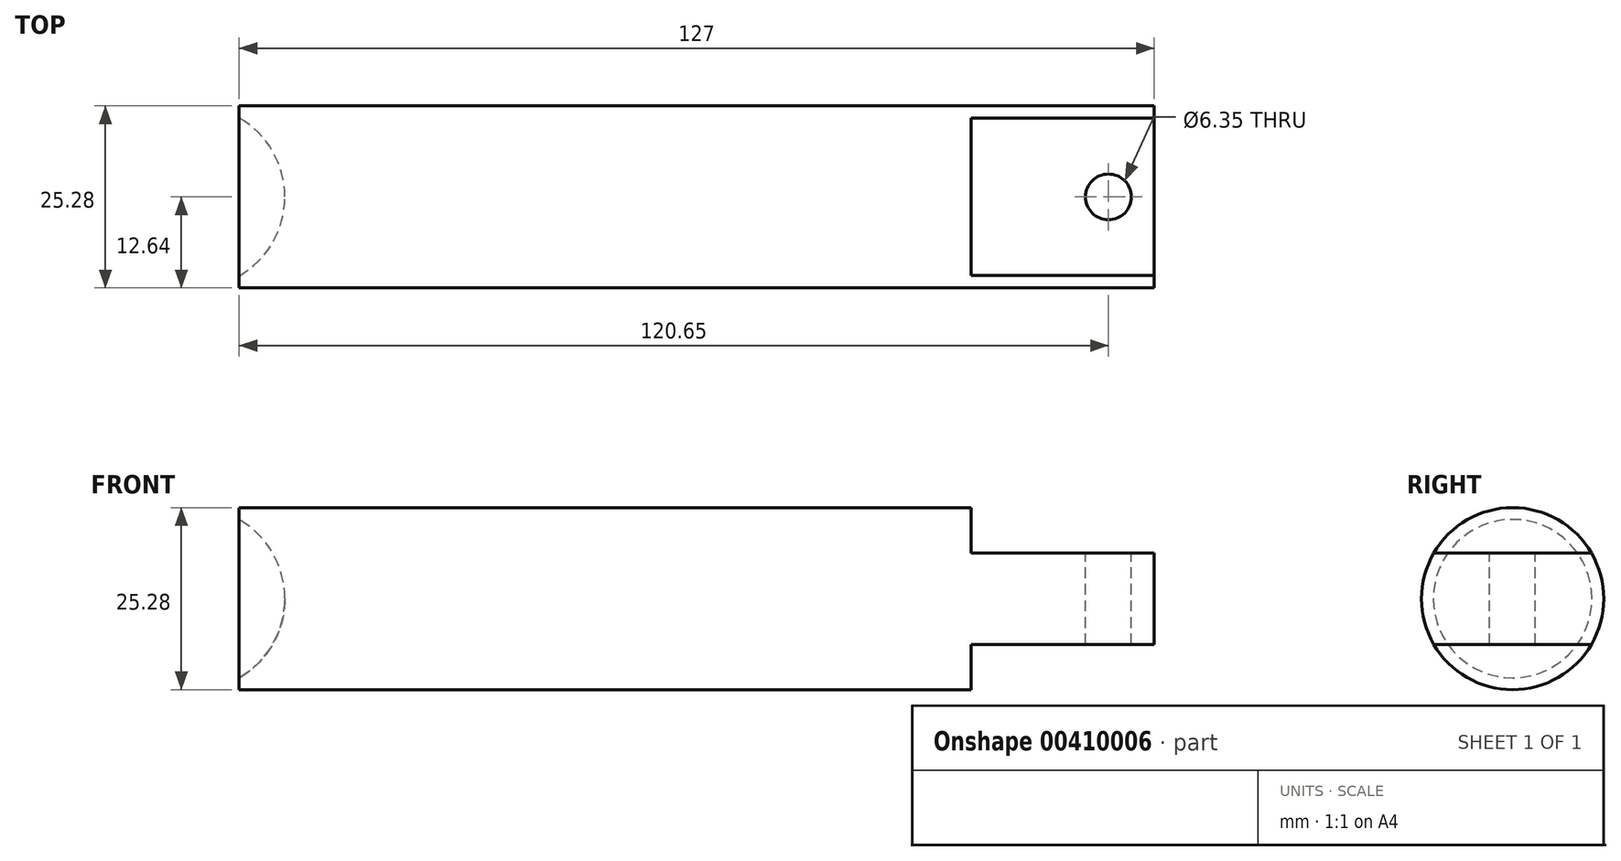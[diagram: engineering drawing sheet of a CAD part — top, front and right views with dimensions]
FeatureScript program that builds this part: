
annotation { "Feature Type Name" : "Feature", "Feature Type Description" : "" }
export const myFeature = defineFeature(function(context is Context, id is Id, definition is map)
    precondition{}
    {
        {
            var Q0;
            Q0=qCreatedBy(makeId("Right.planeOp"),FACE);
            var sketch = newSketch(context, id + "F0", { "sketchPlane" : qUnion([Q0])});
            skCircle(sketch, "E0", {"center": v(0, 0) * mm, "radius": 12.64 * mm});
            skSolve(sketch);
        }
        {
            var Q0;
            Q0 = qSketchRegion(id + "F0", true);
            extrude(context, id + "F1", {"entities" : qUnion([Q0]), "oppositeDirection" : true, "depth" : 127 * mm});
        }
        {
            var Q0;
            Q0=qCreatedBy(makeId("Front.planeOp"),FACE);
            var sketch = newSketch(context, id + "F2", { "sketchPlane" : qUnion([Q0])});
            skLineSegment(sketch, "E1", {"start": v(15.09, 0) * mm, "end": v(-152.6, 0) * mm, "construction": true});
            skLineSegment(sketch, "E2.bottom", {"start": v(0, 6.35) * mm, "end": v(-25.4, 6.35) * mm});
            skLineSegment(sketch, "E2.top", {"start": v(0, 16.72) * mm, "end": v(-25.4, 16.72) * mm});
            skLineSegment(sketch, "E2.left", {"start": v(0, 6.35) * mm, "end": v(0, 16.72) * mm});
            skLineSegment(sketch, "E2.right", {"start": v(-25.4, 6.35) * mm, "end": v(-25.4, 16.72) * mm});
            skLineSegment(sketch, "E3.MirrorCS", {"start": v(0, -6.35) * mm, "end": v(-25.4, -6.35) * mm});
            skLineSegment(sketch, "E4.MirrorCS", {"start": v(-25.4, -6.35) * mm, "end": v(-25.4, -16.72) * mm});
            skLineSegment(sketch, "E5.MirrorCS", {"start": v(0, -16.72) * mm, "end": v(-25.4, -16.72) * mm});
            skLineSegment(sketch, "E6.MirrorCS", {"start": v(0, -6.35) * mm, "end": v(0, -16.72) * mm});
            skSolve(sketch);
        }
        {
            var Q0;
            Q0=makeQuery(id+"F2.imprint","IMPRINT",FACE,{"disambiguationData":[TD([[makeQuery(id+"F2.imprint","IMPRINT",EDGE,{"derivedFrom":sQuery(id+"F2.wireOp",EDGE,"E2.bottom")}),-1.0]])]});
            var Q1;
            Q1=makeQuery(id+"F2.imprint","IMPRINT",FACE,{"disambiguationData":[TD([[makeQuery(id+"F2.imprint","IMPRINT",EDGE,{"derivedFrom":sQuery(id+"F2.wireOp",EDGE,"E3.MirrorCS")}),1.0]])]});
            extrude(context, id + "F3", {"entities" : qUnion([Q0, Q1]), "operationType" : NewBodyOperationType.REMOVE, "endBound" : BoundingType.SYMMETRIC, "oppositeDirection" : true, "depth" : 25.4 * mm});
        }
        {
            var Q0;
            Q0=qCreatedBy(makeId("Top.planeOp"),FACE);
            var sketch = newSketch(context, id + "F4", { "sketchPlane" : qUnion([Q0])});
            skCircle(sketch, "E7", {"center": v(-6.35, 0) * mm, "radius": 3.18 * mm});
            skSolve(sketch);
        }
        {
            var Q0;
            Q0 = qSketchRegion(id + "F4", true);
            extrude(context, id + "F5", {"entities" : qUnion([Q0]), "operationType" : NewBodyOperationType.REMOVE, "endBound" : BoundingType.SYMMETRIC, "oppositeDirection" : true, "depth" : 25.4 * mm});
        }
        {
            var Q0;
            Q0=qCreatedBy(makeId("Front.planeOp"),FACE);
            var sketch = newSketch(context, id + "F6", { "sketchPlane" : qUnion([Q0])});
            skLineSegment(sketch, "E8", {"start": v(4.09, 0) * mm, "end": v(-157.48, 0) * mm, "construction": true});
            skArc(sketch, "E9", {"start": v(-120.65, 0) * mm, "mid": v(-133.35, 12.7) * mm, "end": v(-146.05, 0) * mm});
            skLineSegment(sketch, "E10", {"start": v(-146.05, 0) * mm, "end": v(-120.65, 0) * mm});
            skSolve(sketch);
        }
        {
            var Q0;
            Q0=makeQuery(id+"F6.imprint","IMPRINT",FACE,{"disambiguationData":[TD([[makeQuery(id+"F6.imprint","IMPRINT",EDGE,{"derivedFrom":sQuery(id+"F6.wireOp",EDGE,"E9")}),1.0]])]});
            var Q1;
            Q1=sQuery(id+"F6.wireOp",EDGE,"E8");
            revolve(context, id + "F7", {"operationType" : NewBodyOperationType.REMOVE, "entities" : qUnion([Q0]), "axis" : qUnion([Q1]), "revolveType" : RevolveType.FULL, "oppositeDirection" : true});
        }
    });
